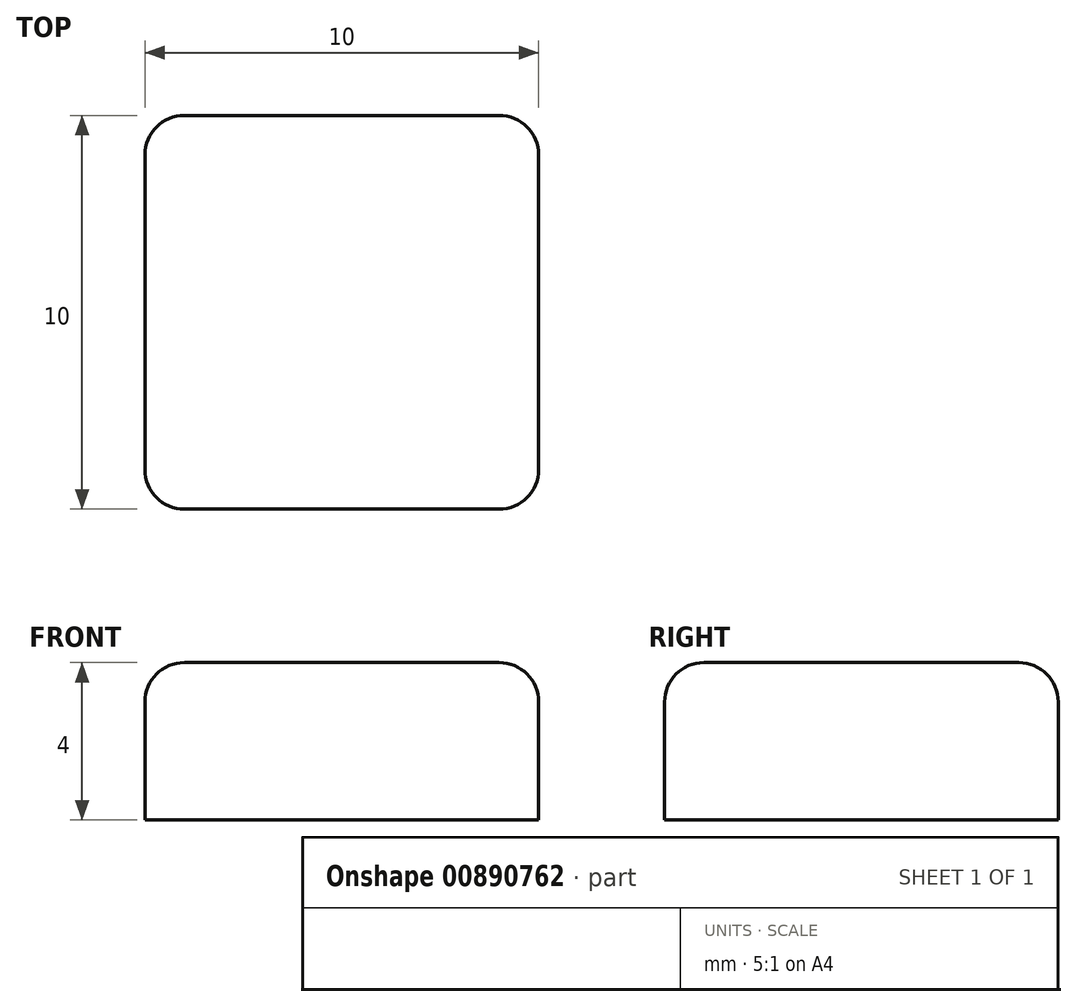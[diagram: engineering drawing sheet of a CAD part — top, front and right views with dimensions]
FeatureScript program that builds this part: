
annotation { "Feature Type Name" : "Feature", "Feature Type Description" : "" }
export const myFeature = defineFeature(function(context is Context, id is Id, definition is map)
    precondition{}
    {
        {
            var Q0;
            Q0=qCreatedBy(makeId("Top.planeOp"),FACE);
            var sketch = newSketch(context, id + "F0", { "sketchPlane" : qUnion([Q0])});
            skLineSegment(sketch, "E0.bottom", {"start": v(5, -5) * mm, "end": v(-5, -5) * mm});
            skLineSegment(sketch, "E0.top", {"start": v(5, 5) * mm, "end": v(-5, 5) * mm});
            skLineSegment(sketch, "E0.left", {"start": v(5, -5) * mm, "end": v(5, 5) * mm});
            skLineSegment(sketch, "E0.right", {"start": v(-5, -5) * mm, "end": v(-5, 5) * mm});
            skPoint(sketch, "E0.middle", {"position": v(0, 0) * mm});
            skSolve(sketch);
        }
        {
            var Q0;
            Q0 = qSketchRegion(id + "F0", true);
            extrude(context, id + "F1", {"entities" : qUnion([Q0]), "depth" : 4 * mm, "offsetDistance" : 25 * mm});
        }
        {
            var Q0;
            Q0=makeQuery(id+"F1.opExtrude","CAP_EDGE",EDGE,{"disambiguationData":[OSD([sQuery(id+"F0.wireOp",EDGE,"E0.left")])],"isStart":false});
            var Q1;
            Q1=makeQuery(id+"F1.opExtrude","CAP_EDGE",EDGE,{"disambiguationData":[OSD([sQuery(id+"F0.wireOp",EDGE,"E0.right")])],"isStart":false});
            var Q2;
            Q2=makeQuery(id+"F1.opExtrude","CAP_FACE",FACE,{"disambiguationData":[OSD([sQuery(id+"F0.wireOp",EDGE,"E0.bottom"),sQuery(id+"F0.wireOp",EDGE,"E0.top"),sQuery(id+"F0.wireOp",EDGE,"E0.left"),sQuery(id+"F0.wireOp",EDGE,"E0.right")])],"isStart":false});
            var Q3;
            Q3=makeQuery(id+"F1.opExtrude","SWEPT_EDGE",EDGE,{"disambiguationData":[OSD([sQuery(id+"F0.wireOp",EDGE,"E0.bottom"),sQuery(id+"F0.wireOp",EDGE,"E0.left")])]});
            var Q4;
            Q4=makeQuery(id+"F1.opExtrude","SWEPT_EDGE",EDGE,{"disambiguationData":[OSD([sQuery(id+"F0.wireOp",EDGE,"E0.bottom"),sQuery(id+"F0.wireOp",EDGE,"E0.right")])]});
            var Q5;
            Q5=makeQuery(id+"F1.opExtrude","SWEPT_EDGE",EDGE,{"disambiguationData":[OSD([sQuery(id+"F0.wireOp",EDGE,"E0.top"),sQuery(id+"F0.wireOp",EDGE,"E0.left")])]});
            var Q6;
            Q6=makeQuery(id+"F1.opExtrude","SWEPT_EDGE",EDGE,{"disambiguationData":[OSD([sQuery(id+"F0.wireOp",EDGE,"E0.top"),sQuery(id+"F0.wireOp",EDGE,"E0.right")])]});
            fillet(context, id + "F2", {"entities" : qUnion([Q0, Q1, Q2, Q3, Q4, Q5, Q6]), "radius" : 1 * mm, "tangentPropagation" : true, "allowEdgeOverflow" : false});
        }
    });
